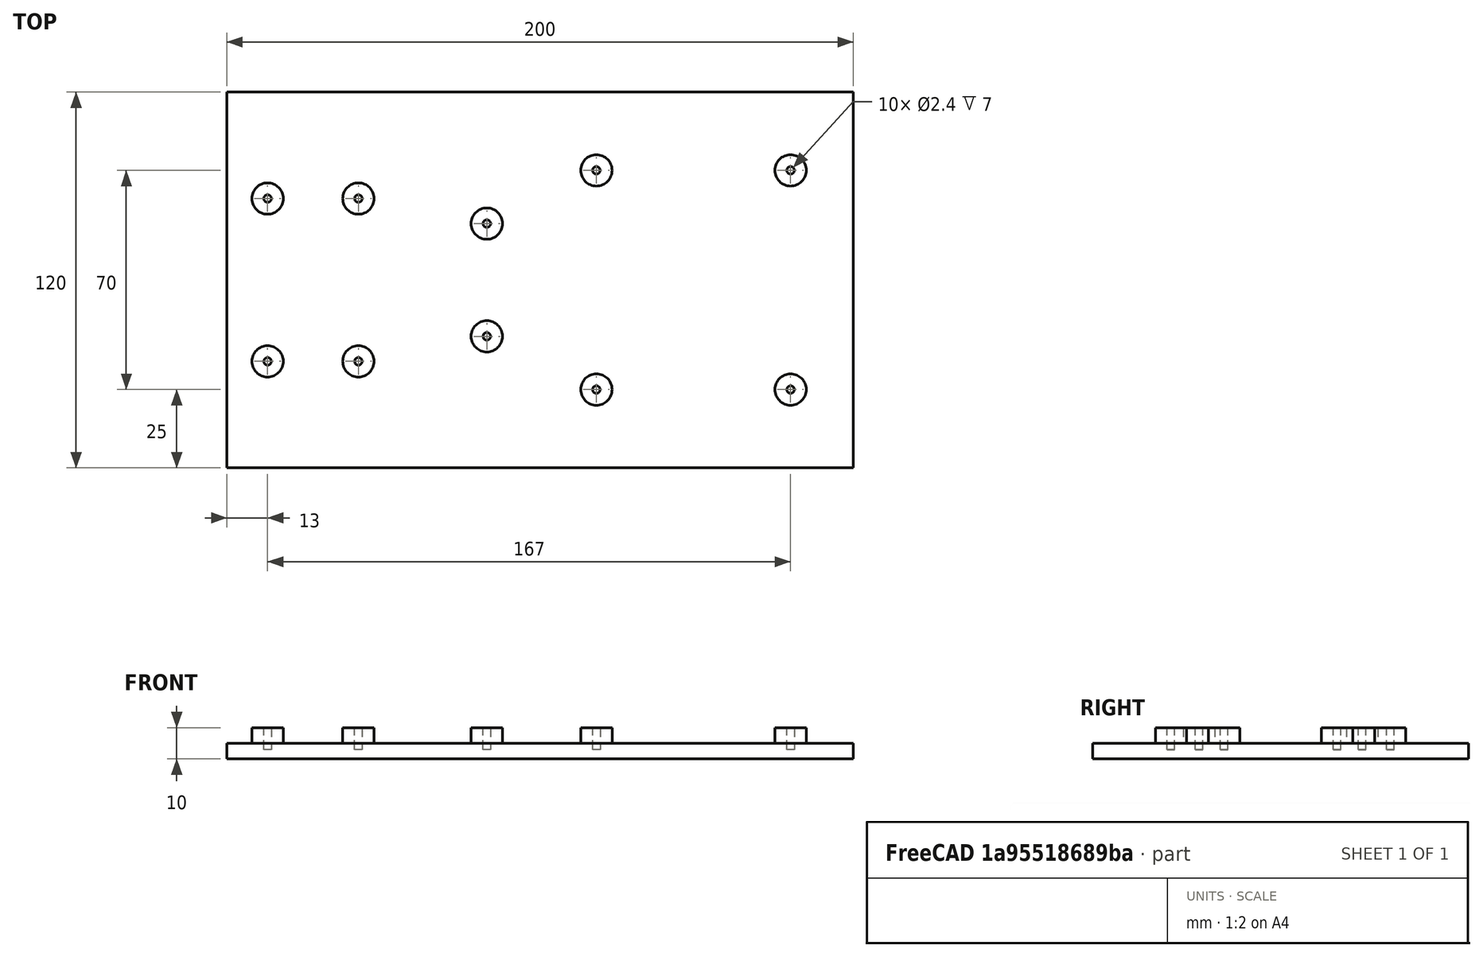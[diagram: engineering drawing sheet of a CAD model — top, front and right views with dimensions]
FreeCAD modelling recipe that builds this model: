
FCSTD DOCUMENT  (FreeCAD 0.20R29410 (Git))
Label: bia_plate
License: All rights reserved
LicenseURL: http://en.wikipedia.org/wiki/All_rights_reserved
objects: Sketcher::SketchObject×3, PartDesign::Pad×2, PartDesign::Pocket×1, PartDesign::Body×1, Mesh::Feature×1
note: 10 computed .brp shape members not serialized (recipe doc carries the construction recipe); baked Part::Feature solids carry a one-line shape summary decoded from their .brp

FEATURE [Sketcher::SketchObject] Sketch
  FullyConstrained = true
  MapMode = 5
  Support = -> [XY_Plane]
  sketch-geometry (4):
    g0: LineSegment StartX=-100 StartY=60 StartZ=0 EndX=100 EndY=60 EndZ=0
    g1: LineSegment StartX=100 StartY=60 StartZ=0 EndX=100 EndY=-60 EndZ=0
    g2: LineSegment StartX=100 StartY=-60 StartZ=0 EndX=-100 EndY=-60 EndZ=0
    g3: LineSegment StartX=-100 StartY=-60 StartZ=0 EndX=-100 EndY=60 EndZ=0
  constraints (12):
    c: Coincident(g0,g1)
    c: Coincident(g1,g2)
    c: Coincident(g2,g3)
    c: Coincident(g3,g0)
    c: Horizontal(g0)
    c: Horizontal(g2)
    c: Vertical(g1)
    c: Vertical(g3)
    c: DistanceX(g0,g0) = 200
    c: DistanceX(g-1,g0) = 100
    c: DistanceY(g1,g1) = 120
    c: DistanceY(g2,g-1) = 60
FEATURE [PartDesign::Pad] Pad
  Direction = (1,1,1)
  Length = 5
  Length2 = 100
  Profile = -> Sketch
  Type = 0
FEATURE [Sketcher::SketchObject] Sketch001
  FullyConstrained = true
  MapMode = 5
  Placement = pos=(0,0,5) rot=(0,0,1;0rad)
  Support = -> [Pad]
  sketch-geometry (10):
    g0: Circle CenterX=18 CenterY=35 CenterZ=0 NormalX=0 NormalY=0 NormalZ=1 AngleXU=0 Radius=5
    g1: Circle CenterX=80 CenterY=35 CenterZ=0 NormalX=0 NormalY=0 NormalZ=1 AngleXU=0 Radius=5
    g2: Circle CenterX=18 CenterY=-35 CenterZ=0 NormalX=0 NormalY=0 NormalZ=1 AngleXU=0 Radius=5
    g3: Circle CenterX=80 CenterY=-35 CenterZ=0 NormalX=0 NormalY=0 NormalZ=1 AngleXU=0 Radius=5
    g4: Circle CenterX=-87 CenterY=26 CenterZ=0 NormalX=0 NormalY=0 NormalZ=1 AngleXU=0 Radius=5
    g5: Circle CenterX=-58 CenterY=26 CenterZ=0 NormalX=0 NormalY=0 NormalZ=1 AngleXU=0 Radius=5
    g6: Circle CenterX=-87 CenterY=-26 CenterZ=0 NormalX=0 NormalY=0 NormalZ=1 AngleXU=0 Radius=5
    g7: Circle CenterX=-58 CenterY=-26 CenterZ=0 NormalX=0 NormalY=0 NormalZ=1 AngleXU=0 Radius=5
    g8: Circle CenterX=-17 CenterY=-18 CenterZ=0 NormalX=0 NormalY=0 NormalZ=1 AngleXU=0 Radius=5
    g9: Circle CenterX=-17 CenterY=18 CenterZ=0 NormalX=0 NormalY=0 NormalZ=1 AngleXU=0 Radius=5
  constraints (30):
    c: Radius(g0) = 5
    c: Equal(g1,g0)
    c: Equal(g3,g0)
    c: Equal(g2,g0)
    c: Equal(g9,g8)
    c: Equal(g4,g5)
    c: Equal(g4,g7)
    c: Equal(g4,g6)
    c: Radius(g4) = 5
    c: Radius(g9) = 5
    c: DistanceX(g0,g1) = 62
    c: DistanceY(g3,g1) = 70
    c: DistanceY(g1,g0) = 0
    c: DistanceX(g2,g3) = 62
    c: DistanceY(g2,g3) = 0
    c: DistanceX(g3,g1) = 0
    c: DistanceX(g8,g9) = 0
    c: DistanceX(g4,g5) = 29
    c: DistanceX(g6,g7) = 29
    c: DistanceY(g4,g5) = 0
    c: DistanceY(g7,g6) = 0
    c: DistanceY(g7,g5) = 52
    c: DistanceX(g7,g5) = 0
    c: DistanceY(g8,g9) = 36
    c: DistanceY(g-1,g9) = 18
    c: DistanceX(g-1,g8) = -17
    c: DistanceX(g-1,g1) = 80
    c: DistanceY(g-1,g1) = 35
    c: DistanceY(g-1,g5) = 26
    c: DistanceX(g5,g-1) = 58
FEATURE [PartDesign::Pad] Pad001
  BaseFeature = -> Pad
  Direction = (0,0,1)
  Length = 5
  Length2 = 100
  Profile = -> Sketch001
  Type = 0
FEATURE [Sketcher::SketchObject] Sketch002
  FullyConstrained = true
  MapMode = 5
  Placement = pos=(0,0,10) rot=(0,0,1;0rad)
  Support = -> [Pad001]
  sketch-geometry (10):
    g0: Circle CenterX=-87 CenterY=26 CenterZ=0 NormalX=0 NormalY=0 NormalZ=1 AngleXU=0 Radius=1.2
    g1: Circle CenterX=-58 CenterY=26 CenterZ=0 NormalX=0 NormalY=0 NormalZ=1 AngleXU=0 Radius=1.2
    g2: Circle CenterX=18 CenterY=35 CenterZ=0 NormalX=0 NormalY=0 NormalZ=1 AngleXU=0 Radius=1.2
    g3: Circle CenterX=80 CenterY=35 CenterZ=0 NormalX=0 NormalY=0 NormalZ=1 AngleXU=0 Radius=1.2
    g4: Circle CenterX=-17 CenterY=18 CenterZ=0 NormalX=0 NormalY=0 NormalZ=1 AngleXU=0 Radius=1.2
    g5: Circle CenterX=-17 CenterY=-18 CenterZ=0 NormalX=0 NormalY=0 NormalZ=1 AngleXU=0 Radius=1.2
    g6: Circle CenterX=80 CenterY=-35 CenterZ=0 NormalX=0 NormalY=0 NormalZ=1 AngleXU=0 Radius=1.2
    g7: Circle CenterX=18 CenterY=-35 CenterZ=0 NormalX=0 NormalY=0 NormalZ=1 AngleXU=0 Radius=1.2
    g8: Circle CenterX=-58 CenterY=-26 CenterZ=0 NormalX=0 NormalY=0 NormalZ=1 AngleXU=0 Radius=1.2
    g9: Circle CenterX=-87 CenterY=-26 CenterZ=0 NormalX=0 NormalY=0 NormalZ=1 AngleXU=0 Radius=1.2
  constraints (30):
    c: Radius(g3) = 1.2
    c: Radius(g4) = 1.2
    c: Radius(g0) = 1.2
    c: Equal(g0,g1)
    c: Equal(g0,g9)
    c: Equal(g0,g8)
    c: Equal(g3,g2)
    c: Equal(g3,g7)
    c: Equal(g3,g6)
    c: Equal(g4,g5)
    c: DistanceX(g2,g3) = 62
    c: DistanceY(g3,g2) = 0
    c: DistanceX(g7,g6) = 62
    c: DistanceY(g7,g6) = 0
    c: DistanceX(g3,g6) = 0
    c: DistanceY(g6,g3) = 70
    c: DistanceY(g-1,g3) = 35
    c: DistanceX(g-1,g3) = 80
    c: DistanceX(g0,g1) = 29
    c: DistanceY(g1,g0) = 0
    c: DistanceY(g8,g1) = 52
    c: DistanceX(g1,g8) = 0
    c: DistanceX(g9,g8) = 29
    c: DistanceY(g9,g8) = 0
    c: DistanceY(g-1,g1) = 26
    c: DistanceX(g1,g-1) = 58
    c: DistanceX(g-1,g4) = -17
    c: DistanceX(g5,g4) = 0
    c: DistanceY(g-1,g4) = 18
    c: DistanceY(g5,g4) = 36
FEATURE [PartDesign::Pocket] Pocket
  BaseFeature = -> Pad001
  Direction = (0,0,-1)
  Length = 7
  Length2 = 100
  Profile = -> Sketch002
  Type = 0
FEATURE [PartDesign::Body] Body  label="bia_plate"
  Group = -> [Sketch,Pad,Sketch001,Pad001,Sketch002,Pocket]
  Origin = -> Origin
  Tip = -> Pocket
FEATURE [Mesh::Feature] Mesh  label="bia_plate (Meshed)"
